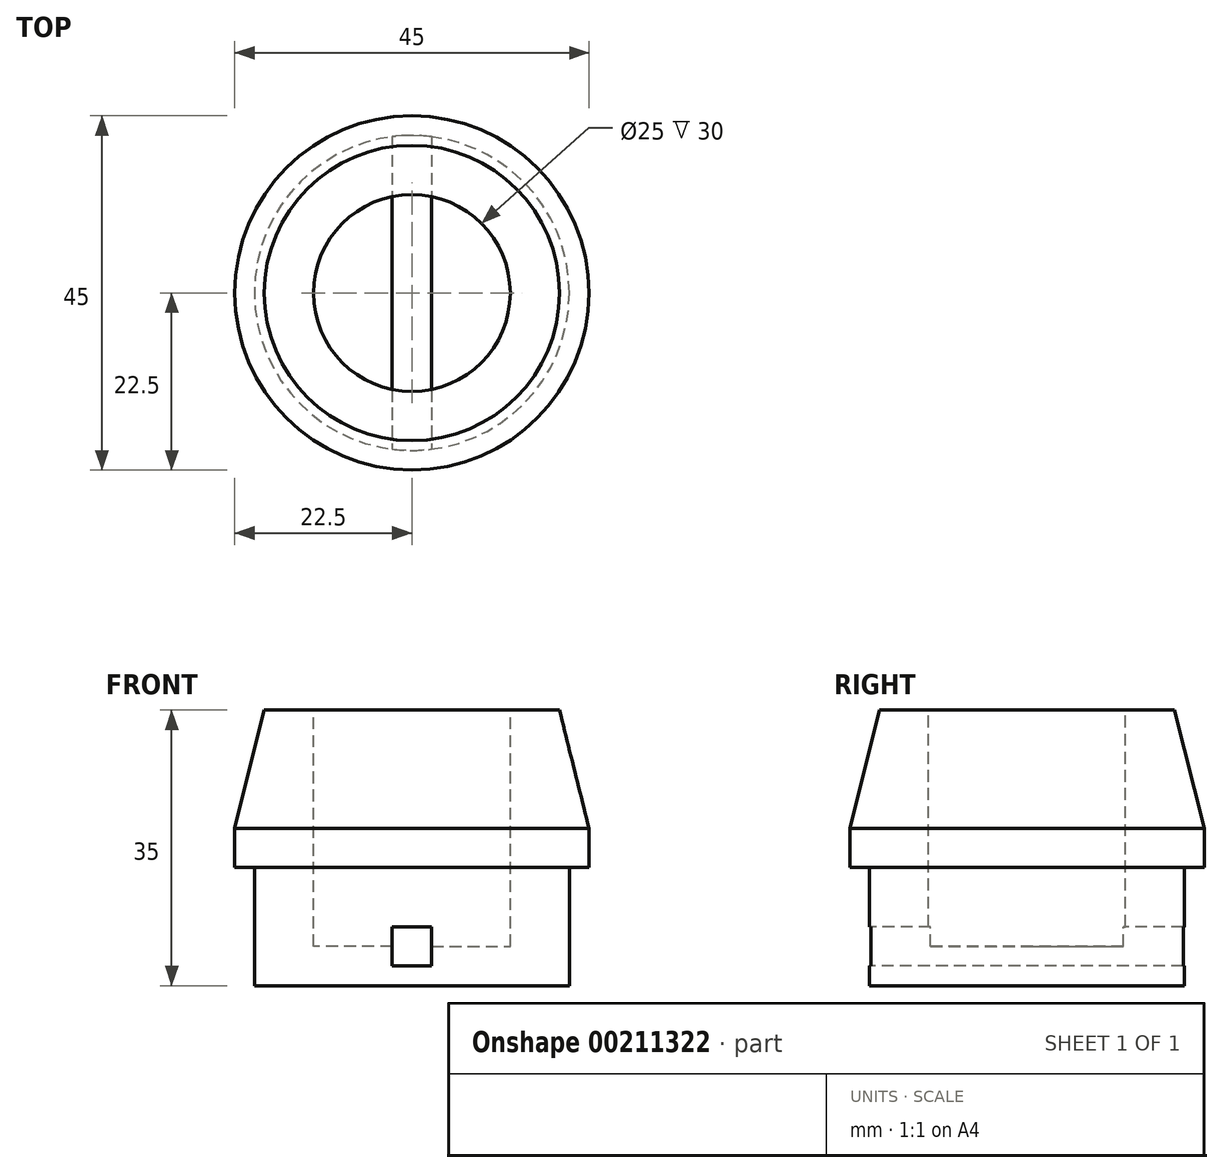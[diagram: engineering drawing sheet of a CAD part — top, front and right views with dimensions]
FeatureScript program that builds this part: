
annotation { "Feature Type Name" : "Feature", "Feature Type Description" : "" }
export const myFeature = defineFeature(function(context is Context, id is Id, definition is map)
    precondition{}
    {
        {
            var Q0;
            Q0=qCreatedBy(makeId("Top.planeOp"),FACE);
            var sketch = newSketch(context, id + "F0", { "sketchPlane" : qUnion([Q0])});
            skCircle(sketch, "E0", {"center": v(0, 0) * mm, "radius": 22.5 * mm});
            skSolve(sketch);
        }
        {
            var Q0;
            Q0=makeQuery(id+"F0.imprint","IMPRINT",FACE,{"disambiguationData":[TD([[makeQuery(id+"F0.imprint","IMPRINT",EDGE,{"derivedFrom":sQuery(id+"F0.wireOp",EDGE,"E0")}),1.0]])]});
            extrude(context, id + "F1", {"entities" : qUnion([Q0]), "depth" : 25 * mm});
        }
        {
            var Q0;
            Q0=makeQuery(id+"F1.opExtrude","CAP_FACE",FACE,{"disambiguationData":[OSD([sQuery(id+"F0.wireOp",EDGE,"E0")])],"isStart":true});
            var sketch = newSketch(context, id + "F2", { "sketchPlane" : qUnion([Q0])});
            skCircle(sketch, "E1", {"center": v(0, 0) * mm, "radius": 20 * mm});
            skSolve(sketch);
        }
        {
            var Q0;
            Q0=makeQuery(id+"F2.imprint","IMPRINT",FACE,{"disambiguationData":[TD([[makeQuery(id+"F2.imprint","IMPRINT",EDGE,{"derivedFrom":sQuery(id+"F2.wireOp",EDGE,"E1")}),-1.0]])]});
            extrude(context, id + "F3", {"entities" : qUnion([Q0]), "operationType" : NewBodyOperationType.REMOVE, "oppositeDirection" : true, "depth" : 5 * mm});
        }
        {
            var Q0;
            Q0=qCreatedBy(makeId("Front.planeOp"),FACE);
            var sketch = newSketch(context, id + "F4", { "sketchPlane" : qUnion([Q0])});
            skLineSegment(sketch, "E2", {"start": v(0, 0) * mm, "end": v(0, 10) * mm});
            skLineSegment(sketch, "E3", {"start": v(0, 10) * mm, "end": v(-22.5, 10) * mm});
            skLineSegment(sketch, "E4", {"start": v(0, 0) * mm, "end": v(0, 30) * mm});
            skLineSegment(sketch, "E5", {"start": v(0, 30) * mm, "end": v(-12.5, 30) * mm});
            skLineSegment(sketch, "E6", {"start": v(-12.5, 30) * mm, "end": v(-17.5, 30) * mm});
            skLineSegment(sketch, "E7", {"start": v(-17.5, 30) * mm, "end": v(-22.5, 10) * mm});
            skLineSegment(sketch, "E8", {"start": v(-17.5, 30) * mm, "end": v(-22.5, 30) * mm});
            skLineSegment(sketch, "E9", {"start": v(-22.5, 30) * mm, "end": v(-22.5, 10) * mm});
            skSolve(sketch);
        }
        {
            var Q0;
            Q0=makeQuery(id+"F4.imprint","IMPRINT",FACE,{"disambiguationData":[TD([[makeQuery(id+"F4.imprint","IMPRINT",EDGE,{"derivedFrom":sQuery(id+"F4.wireOp",EDGE,"E7")}),-1.0]])]});
            var Q1;
            Q1=sQuery(id+"F4.wireOp",EDGE,"E4");
            revolve(context, id + "F5", {"operationType" : NewBodyOperationType.REMOVE, "entities" : qUnion([Q0]), "axis" : qUnion([Q1]), "revolveType" : RevolveType.FULL, "oppositeDirection" : true});
        }
        {
            var Q0;
            Q0=makeQuery(id+"F1.opExtrude","CAP_FACE",FACE,{"disambiguationData":[OSD([sQuery(id+"F0.wireOp",EDGE,"E0")])],"isStart":false});
            var sketch = newSketch(context, id + "F6", { "sketchPlane" : qUnion([Q0])});
            skCircle(sketch, "E10", {"center": v(0, 0) * mm, "radius": 12.5 * mm});
            skSolve(sketch);
        }
        {
            var Q0;
            Q0=makeQuery(id+"F1.opExtrude","CAP_FACE",FACE,{"disambiguationData":[OSD([sQuery(id+"F0.wireOp",EDGE,"E0")])],"isStart":true});
            extrude(context, id + "F7", {"entities" : qUnion([Q0]), "operationType" : NewBodyOperationType.ADD, "depth" : 10 * mm});
        }
        {
            var Q0;
            Q0=makeQuery(id+"F6.imprint","IMPRINT",FACE,{"disambiguationData":[TD([[makeQuery(id+"F6.imprint","IMPRINT",EDGE,{"derivedFrom":sQuery(id+"F6.wireOp",EDGE,"E10")}),1.0]])]});
            extrude(context, id + "F8", {"entities" : qUnion([Q0]), "operationType" : NewBodyOperationType.REMOVE, "oppositeDirection" : true, "depth" : 30 * mm});
        }
        {
            var Q0;
            Q0=qCreatedBy(makeId("Front.planeOp"),FACE);
            var sketch = newSketch(context, id + "F9", { "sketchPlane" : qUnion([Q0])});
            skLineSegment(sketch, "E11", {"start": v(0, 0) * mm, "end": v(0, -10) * mm});
            skLineSegment(sketch, "E12", {"start": v(0, -10) * mm, "end": v(0, -5) * mm});
            skLineSegment(sketch, "E13.bottom", {"start": v(2.5, -7.5) * mm, "end": v(-2.5, -7.5) * mm});
            skLineSegment(sketch, "E13.top", {"start": v(2.5, -2.5) * mm, "end": v(-2.5, -2.5) * mm});
            skLineSegment(sketch, "E13.left", {"start": v(2.5, -7.5) * mm, "end": v(2.5, -2.5) * mm});
            skLineSegment(sketch, "E13.right", {"start": v(-2.5, -7.5) * mm, "end": v(-2.5, -2.5) * mm});
            skPoint(sketch, "E13.middle", {"position": v(0, -5) * mm});
            skSolve(sketch);
        }
        {
            var Q0;
            Q0 = qSketchRegion(id + "F9", true);
            extrude(context, id + "F10", {"entities" : qUnion([Q0]), "operationType" : NewBodyOperationType.REMOVE, "endBound" : BoundingType.SYMMETRIC, "oppositeDirection" : true, "depth" : 50 * mm});
        }
    });
